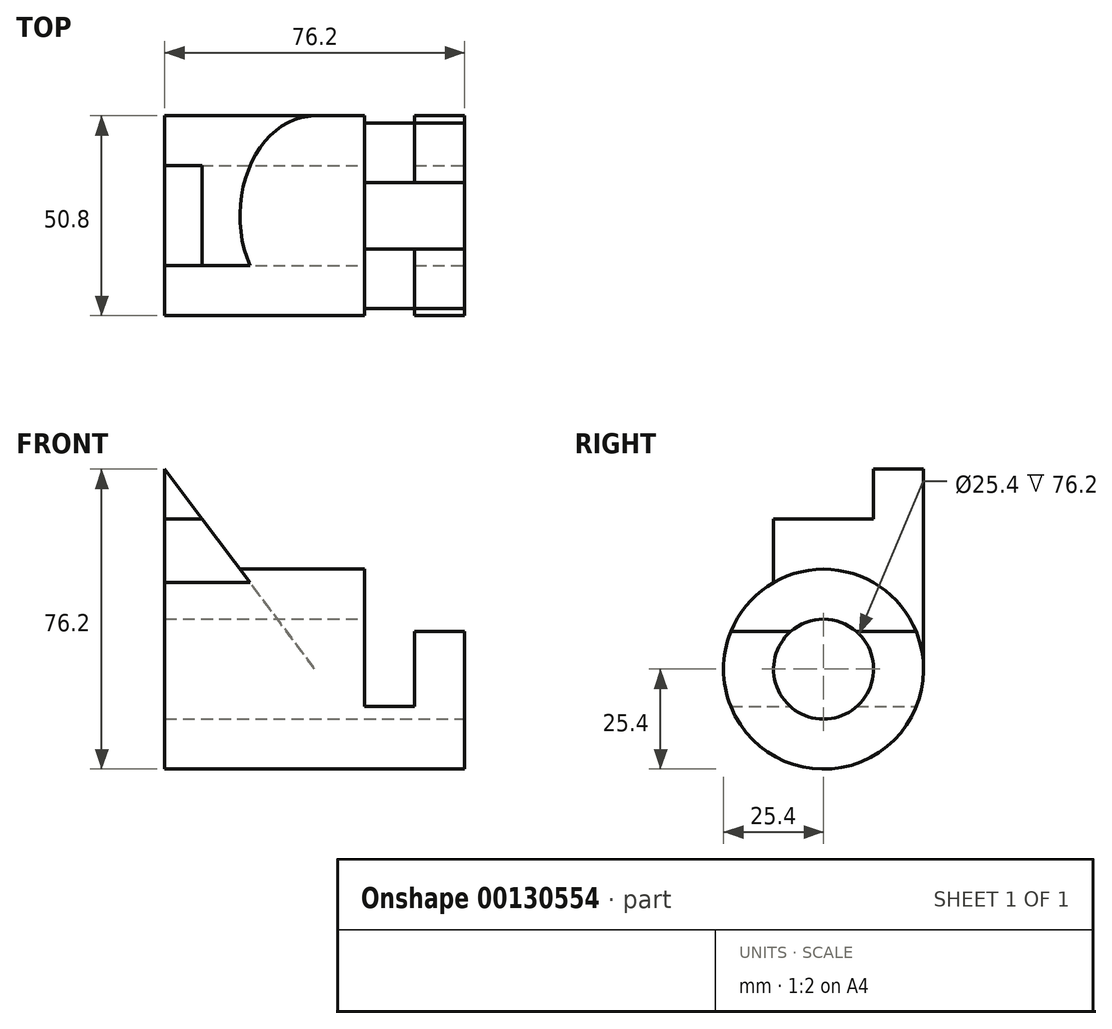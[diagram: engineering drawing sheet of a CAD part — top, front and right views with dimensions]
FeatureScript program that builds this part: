
annotation { "Feature Type Name" : "Feature", "Feature Type Description" : "" }
export const myFeature = defineFeature(function(context is Context, id is Id, definition is map)
    precondition{}
    {
        {
            var Q0;
            Q0=qCreatedBy(makeId("Right.planeOp"),FACE);
            var sketch = newSketch(context, id + "F0", { "sketchPlane" : qUnion([Q0])});
            skCircle(sketch, "E0", {"center": v(0, 0) * mm, "radius": 12.7 * mm});
            skCircle(sketch, "E1", {"center": v(0, 0) * mm, "radius": 25.4 * mm});
            skSolve(sketch);
        }
        {
            var Q0;
            Q0 = qSketchRegion(id + "F0", true);
            extrude(context, id + "F1", {"entities" : qUnion([Q0]), "oppositeDirection" : true, "depth" : 76.2 * mm});
        }
        {
            var Q0;
            Q0=qCreatedBy(makeId("Front.planeOp"),FACE);
            var sketch = newSketch(context, id + "F2", { "sketchPlane" : qUnion([Q0])});
            skLineSegment(sketch, "E2", {"start": v(0, 9.53) * mm, "end": v(-12.7, 9.52) * mm});
            skLineSegment(sketch, "E3", {"start": v(-12.7, 9.52) * mm, "end": v(-12.7, -9.53) * mm});
            skLineSegment(sketch, "E4", {"start": v(-12.7, -9.53) * mm, "end": v(-25.4, -9.53) * mm});
            skLineSegment(sketch, "E5", {"start": v(-25.4, -9.53) * mm, "end": v(-25.4, 25.4) * mm});
            skLineSegment(sketch, "E6", {"start": v(-25.4, 25.4) * mm, "end": v(0, 25.4) * mm});
            skLineSegment(sketch, "E7", {"start": v(0, 25.4) * mm, "end": v(0, 9.53) * mm});
            skSolve(sketch);
        }
        {
            var Q0;
            Q0 = qSketchRegion(id + "F2", true);
            extrude(context, id + "F3", {"entities" : qUnion([Q0]), "operationType" : NewBodyOperationType.REMOVE, "endBound" : BoundingType.SYMMETRIC, "depth" : 50.8 * mm});
        }
        {
            var Q0;
            Q0=makeQuery(id+"F1.opExtrude","CAP_FACE",FACE,{"disambiguationData":[OSD([sQuery(id+"F0.wireOp",EDGE,"E0"),sQuery(id+"F0.wireOp",EDGE,"E1")])],"isStart":false});
            var sketch = newSketch(context, id + "F4", { "sketchPlane" : qUnion([Q0])});
            skLineSegment(sketch, "E8", {"start": v(0, 0) * mm, "end": v(-25.4, 0) * mm});
            skLineSegment(sketch, "E9", {"start": v(-25.4, 0) * mm, "end": v(-25.4, 50.8) * mm});
            skLineSegment(sketch, "E10", {"start": v(-25.4, 50.8) * mm, "end": v(-12.7, 50.8) * mm});
            skLineSegment(sketch, "E11", {"start": v(-12.7, 50.8) * mm, "end": v(-12.7, 38.1) * mm});
            skLineSegment(sketch, "E12", {"start": v(-12.7, 38.1) * mm, "end": v(12.7, 38.1) * mm});
            skLineSegment(sketch, "E13", {"start": v(12.7, 38.1) * mm, "end": v(12.7, 0) * mm});
            skLineSegment(sketch, "E14", {"start": v(12.7, 0) * mm, "end": v(0, 0) * mm});
            skSolve(sketch);
        }
        {
            var Q0;
            Q0 = qSketchRegion(id + "F4", true);
            extrude(context, id + "F5", {"entities" : qUnion([Q0]), "operationType" : NewBodyOperationType.ADD, "oppositeDirection" : true, "depth" : 38.1 * mm});
        }
        {
            var Q0;
            Q0=makeQuery(id+"F5.opExtrude","SWEPT_FACE",FACE,{"disambiguationData":[OSD([sQuery(id+"F4.wireOp",EDGE,"E9")])]});
            var sketch = newSketch(context, id + "F6", { "sketchPlane" : qUnion([Q0])});
            skLineSegment(sketch, "E15", {"start": v(38.1, 50.8) * mm, "end": v(76.2, 50.8) * mm});
            skLineSegment(sketch, "E16", {"start": v(76.2, 50.8) * mm, "end": v(38.1, 0) * mm});
            skLineSegment(sketch, "E17", {"start": v(38.1, 0) * mm, "end": v(38.1, 50.8) * mm});
            skSolve(sketch);
        }
        {
            var Q0;
            Q0=makeQuery(id+"F6.imprint","IMPRINT",FACE,{"disambiguationData":[TD([[makeQuery(id+"F6.imprint","IMPRINT",EDGE,{"derivedFrom":sQuery(id+"F6.wireOp",EDGE,"E15")}),-1.0]])]});
            extrude(context, id + "F7", {"entities" : qUnion([Q0]), "operationType" : NewBodyOperationType.REMOVE, "oppositeDirection" : true, "depth" : 50.8 * mm});
        }
        {
            var Q0;
            Q0=makeQuery(id+"F7.boolean.opBoolean","COPY",FACE,{"derivedFrom":makeQuery(id+"F7.opExtrude","SWEPT_FACE",FACE,{"disambiguationData":[OSD([sQuery(id+"F6.wireOp",EDGE,"E17")])]})});
            var Q1;
            Q1=makeQuery(id+"F7.boolean.opBoolean","COPY",FACE,{"derivedFrom":makeQuery(id+"F7.opExtrude","SWEPT_FACE",FACE,{"disambiguationData":[OSD([sQuery(id+"F6.wireOp",EDGE,"E16")])]})});
            extrude(context, id + "F8", {"entities" : qUnion([Q0]), "operationType" : NewBodyOperationType.ADD, "endBound" : BoundingType.UP_TO_SURFACE, "endBoundEntityFace" : qUnion([Q1]), "depth" : 25.4 * mm});
        }
        {
            var Q0;
            Q0=qCreatedBy(makeId("Right.planeOp"),FACE);
            var sketch = newSketch(context, id + "F9", { "sketchPlane" : qUnion([Q0])});
            skCircle(sketch, "E18", {"center": v(0, 0) * mm, "radius": 12.7 * mm});
            skSolve(sketch);
        }
        {
            var Q0;
            Q0 = qSketchRegion(id + "F9", true);
            var Q1;
            Q1=makeQuery(id+"F5.boolean.opBoolean","MERGE",FACE,{"derivedFrom":[makeQuery(id+"F1.opExtrude","CAP_FACE",FACE,{"disambiguationData":[OSD([sQuery(id+"F0.wireOp",EDGE,"E0"),sQuery(id+"F0.wireOp",EDGE,"E1")])],"isStart":false}),makeQuery(id+"F5.opExtrude","CAP_FACE",FACE,{"disambiguationData":[OSD([sQuery(id+"F4.wireOp",EDGE,"E8"),sQuery(id+"F4.wireOp",EDGE,"E9"),sQuery(id+"F4.wireOp",EDGE,"E10"),sQuery(id+"F4.wireOp",EDGE,"E11"),sQuery(id+"F4.wireOp",EDGE,"E12"),sQuery(id+"F4.wireOp",EDGE,"E13"),sQuery(id+"F4.wireOp",EDGE,"E14")])],"isStart":true})]});
            extrude(context, id + "F10", {"entities" : qUnion([Q0]), "operationType" : NewBodyOperationType.REMOVE, "endBound" : BoundingType.UP_TO_SURFACE, "oppositeDirection" : true, "endBoundEntityFace" : qUnion([Q1]), "depth" : 25.4 * mm});
        }
    });
